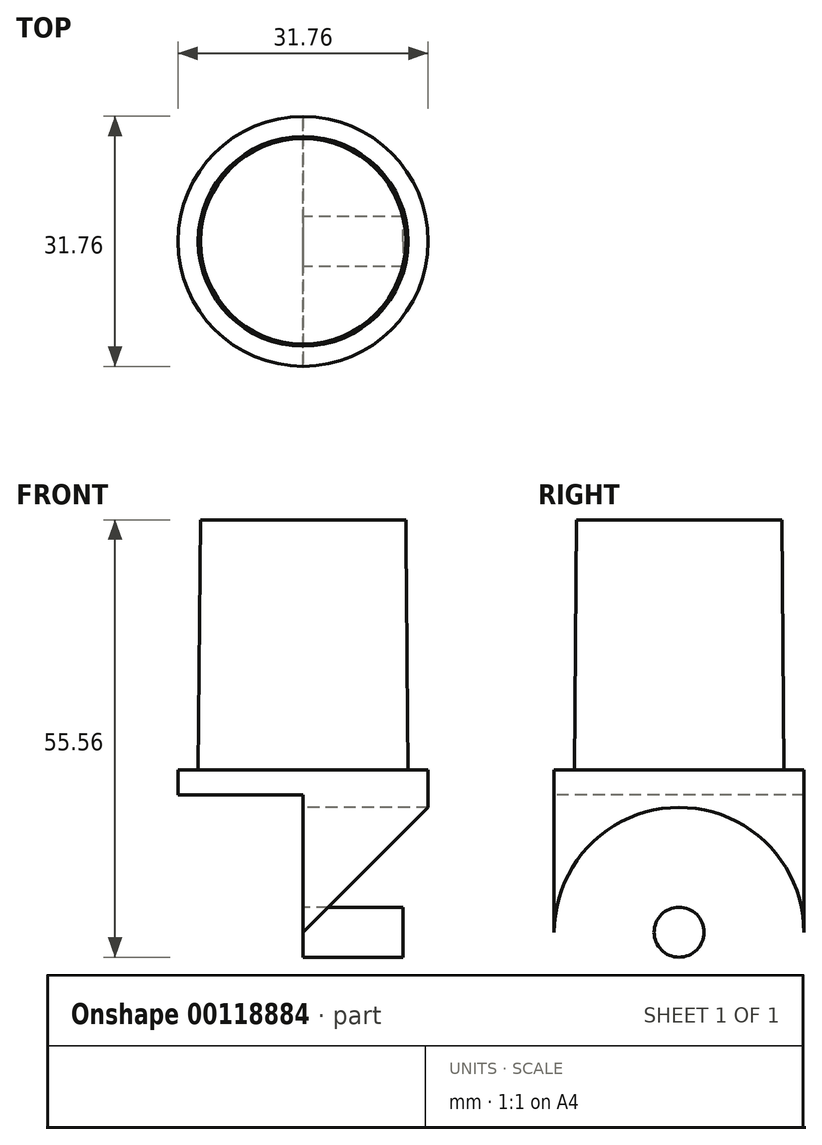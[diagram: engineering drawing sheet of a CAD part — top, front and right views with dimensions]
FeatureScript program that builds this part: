
annotation { "Feature Type Name" : "Feature", "Feature Type Description" : "" }
export const myFeature = defineFeature(function(context is Context, id is Id, definition is map)
    precondition{}
    {
        {
            var Q0;
            Q0=qCreatedBy(makeId("Top.planeOp"),FACE);
            var sketch = newSketch(context, id + "F0", { "sketchPlane" : qUnion([Q0])});
            skCircle(sketch, "E0", {"center": v(0, 0) * mm, "radius": 13.32 * mm});
            skCircle(sketch, "E1", {"center": v(0, 0) * mm, "radius": 15.88 * mm});
            skLineSegment(sketch, "E2", {"start": v(0, 15.88) * mm, "end": v(0, -15.88) * mm});
            skSolve(sketch);
        }
        {
            var Q0;
            Q0=makeQuery(id+"F0.imprint","IMPRINT",FACE,{"disambiguationData":[TD([[makeQuery(id+"F0.imprint","IMPRINT",EDGE,{"derivedFrom":sQuery(id+"F0.wireOp",EDGE,"E0")}),1.0]])]});
            extrude(context, id + "F1", {"entities" : qUnion([Q0]), "depth" : 31.75 * mm, "hasDraft" : true, "draftAngle" : .5 * degree, "draftPullDirection" : true});
        }
        {
            var Q0;
            {var subQ0=sQuery(id+"F0.wireOp",EDGE,"E2");var subQ1=sQuery(id+"F0.wireOp",EDGE,"E0");var subQ2=makeQuery(id+"F0.imprint","INTERSECT",VERTEX,{"disambiguationData":[OD(0.0)],"derivedFrom":[subQ1,subQ0]});Q0=makeQuery(id+"F0.imprint","IMPRINT",FACE,{"disambiguationData":[TD([[makeQuery(id+"F0.imprint","IMPRINT",EDGE,{"disambiguationData":[TD([[subQ2,1.0]])],"derivedFrom":subQ1}),1.0]])]});}
            var Q1;
            {var subQ0=sQuery(id+"F0.wireOp",EDGE,"E2");var subQ1=sQuery(id+"F0.wireOp",EDGE,"E0");var subQ2=makeQuery(id+"F0.imprint","INTERSECT",VERTEX,{"disambiguationData":[OD(0.0)],"derivedFrom":[subQ1,subQ0]});Q1=makeQuery(id+"F0.imprint","IMPRINT",FACE,{"disambiguationData":[TD([[makeQuery(id+"F0.imprint","IMPRINT",EDGE,{"disambiguationData":[TD([[subQ2,1.0]])],"derivedFrom":subQ1}),-1.0]])]});}
            extrude(context, id + "F2", {"entities" : qUnion([Q0, Q1]), "operationType" : NewBodyOperationType.ADD, "oppositeDirection" : true, "depth" : 36.5 * mm});
        }
        {
            var Q0;
            {var subQ0=sQuery(id+"F0.wireOp",EDGE,"E2");var subQ1=sQuery(id+"F0.wireOp",EDGE,"E0");var subQ2=makeQuery(id+"F0.imprint","INTERSECT",VERTEX,{"disambiguationData":[OD(0.0)],"derivedFrom":[subQ1,subQ0]});Q0=makeQuery(id+"F0.imprint","IMPRINT",FACE,{"disambiguationData":[TD([[makeQuery(id+"F0.imprint","IMPRINT",EDGE,{"disambiguationData":[TD([[subQ2,-1.0]])],"derivedFrom":subQ1}),-1.0]])]});}
            var Q1;
            {var subQ0=sQuery(id+"F0.wireOp",EDGE,"E2");var subQ1=sQuery(id+"F0.wireOp",EDGE,"E0");var subQ2=makeQuery(id+"F0.imprint","INTERSECT",VERTEX,{"disambiguationData":[OD(0.0)],"derivedFrom":[subQ1,subQ0]});Q1=makeQuery(id+"F0.imprint","IMPRINT",FACE,{"disambiguationData":[TD([[makeQuery(id+"F0.imprint","IMPRINT",EDGE,{"disambiguationData":[TD([[subQ2,-1.0]])],"derivedFrom":subQ1}),1.0]])]});}
            extrude(context, id + "F3", {"entities" : qUnion([Q0, Q1]), "operationType" : NewBodyOperationType.ADD, "oppositeDirection" : true, "depth" : 3.17 * mm});
        }
        {
            var Q0;
            Q0=makeQuery(id+"F2.opExtrude","SWEPT_FACE",FACE,{"disambiguationData":[OSD([sQuery(id+"F0.wireOp",EDGE,"E2")])]});
            var sketch = newSketch(context, id + "F4", { "sketchPlane" : qUnion([Q0])});
            skCircle(sketch, "E3", {"center": v(0, -20.64) * mm, "radius": 15.88 * mm});
            skLineSegment(sketch, "E4", {"start": v(-15.88, -20.64) * mm, "end": v(15.88, -20.64) * mm});
            skPoint(sketch, "E4.endSnap0", {"position": v(15.88, -19.84) * mm});
            skCircle(sketch, "E5", {"center": v(0, -20.64) * mm, "radius": 3.18 * mm});
            skSolve(sketch);
        }
        {
            var Q0;
            {var subQ0=sQuery(id+"F4.wireOp",EDGE,"E5");var subQ1=sQuery(id+"F4.wireOp",EDGE,"E4");var subQ2=makeQuery(id+"F4.imprint","INTERSECT",VERTEX,{"disambiguationData":[OD(0.0)],"derivedFrom":[subQ1,subQ0]});Q0=makeQuery(id+"F4.imprint","IMPRINT",FACE,{"disambiguationData":[TD([[makeQuery(id+"F4.imprint","IMPRINT",EDGE,{"disambiguationData":[TD([[subQ2,-1.0]])],"derivedFrom":subQ1}),-1.0]])]});}
            var Q1;
            {var subQ0=sQuery(id+"F4.wireOp",EDGE,"E5");var subQ1=sQuery(id+"F4.wireOp",EDGE,"E4");var subQ2=makeQuery(id+"F4.imprint","INTERSECT",VERTEX,{"disambiguationData":[OD(0.0)],"derivedFrom":[subQ1,subQ0]});Q1=makeQuery(id+"F4.imprint","IMPRINT",FACE,{"disambiguationData":[TD([[makeQuery(id+"F4.imprint","IMPRINT",EDGE,{"disambiguationData":[TD([[subQ2,-1.0]])],"derivedFrom":subQ1}),1.0]])]});}
            var Q2;
            {var subQ0=sQuery(id+"F4.wireOp",EDGE,"E3");var subQ1=sQuery(id+"F0.wireOp",EDGE,"E2");var subQ5=makeQuery(id+"F2.opExtrude","CAP_EDGE",EDGE,{"disambiguationData":[OSD([subQ1])],"isStart":false});var subQ6=makeQuery(id+"F4.imprint","INTERSECT",VERTEX,{"derivedFrom":[subQ5,subQ0]});Q2=makeQuery(id+"F4.imprint","IMPRINT",FACE,{"disambiguationData":[TD([[makeQuery(id+"F4.imprint","IMPRINT",EDGE,{"disambiguationData":[TD([[subQ6,1.0]])],"derivedFrom":subQ5}),1.0]])]});}
            var Q3;
            {var subQ0=sQuery(id+"F4.wireOp",EDGE,"E3");var subQ1=sQuery(id+"F0.wireOp",EDGE,"E2");var subQ5=makeQuery(id+"F2.opExtrude","CAP_EDGE",EDGE,{"disambiguationData":[OSD([subQ1])],"isStart":false});var subQ6=makeQuery(id+"F4.imprint","INTERSECT",VERTEX,{"derivedFrom":[subQ5,subQ0]});Q3=makeQuery(id+"F4.imprint","IMPRINT",FACE,{"disambiguationData":[TD([[makeQuery(id+"F4.imprint","IMPRINT",EDGE,{"disambiguationData":[TD([[subQ6,-1.0]])],"derivedFrom":subQ5}),1.0]])]});}
            extrude(context, id + "F5", {"entities" : qUnion([Q0, Q1, Q2, Q3]), "operationType" : NewBodyOperationType.REMOVE, "endBound" : BoundingType.THROUGH_ALL, "oppositeDirection" : true, "depth" : 25.4 * mm});
        }
        {
            var Q0;
            Q0=qCreatedBy(makeId("Right.planeOp"),FACE);
            cPlane(context, id + "F6", {"entities" : qUnion([Q0]), "cplaneType" : CPlaneType.OFFSET, "offset" : 15.88 * mm, "width" : 152.4 * mm, "height" : 152.4 * mm});
        }
        {
            var Q0;
            Q0=qCreatedBy(id+"F6.planeOp",FACE);
            var sketch = newSketch(context, id + "F7", { "sketchPlane" : qUnion([Q0])});
            skCircle(sketch, "E6.0", {"center": v(0, -20.64) * mm, "radius": 3.18 * mm, "construction": true});
            skCircle(sketch, "E7", {"center": v(0, -20.64) * mm, "radius": 6.35 * mm});
            skSolve(sketch);
        }
        {
            var Q0;
            Q0=makeQuery(id+"F7.imprint","IMPRINT",FACE,{"disambiguationData":[TD([[makeQuery(id+"F7.imprint","IMPRINT",EDGE,{"derivedFrom":sQuery(id+"F7.wireOp",EDGE,"E7")}),1.0]])]});
            extrude(context, id + "F8", {"entities" : qUnion([Q0]), "operationType" : NewBodyOperationType.REMOVE, "oppositeDirection" : true, "depth" : 3.17 * mm});
        }
    });
